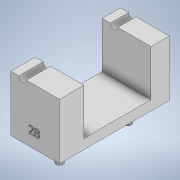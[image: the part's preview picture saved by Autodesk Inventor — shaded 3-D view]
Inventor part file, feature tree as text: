
AUTODESK INVENTOR PART (.ipt)
format: ipt  version: 2021 (Build 250183000, 183)  size: 216,064 bytes
history: native  units: mm
features: sketch x5, extrude x4, emboss x1
ambient origin geometry x8: Origin, YZ Plane, XZ Plane, XY Plane, X Axis, Y Axis, Z Axis, Center Point
bodies: Solid1 (feature_tree)
feature tree (10):
  extrude  "Extrusion1"  Depth=22.877mm
  extrude  "Extrusion2"  Depth=20.0mm TaperAngle=0.0deg
  extrude  "Extrusion3"  Depth=3.0mm
  extrude  "Extrusion4"  Depth=3.5mm
  emboss  "Emboss1"
  sketch  "Sketch1"  dims[d0=45.0mm d1=22.877mm]
  sketch  "Sketch2"  dims[d2=11.4385mm d4=20.0mm d5=0.0mm]
  sketch  "Sketch3"  dims[d6=3.0mm d7=3.0mm]
  sketch  "Sketch4"  dims[d8=28.0mm d10=3.5mm]
  sketch  "Sketch5"  dims[d12=3.5mm d13=3.0mm d14=0.0mm d15=17.5mm d17=7.5mm d18=4.0mm d19=0.0mm d20=0.0mm d21=3.0mm d22=15.113mm d23=0.0mm d24=0.0mm d25=10.0mm d26=1.0mm d27=0.0mm]
